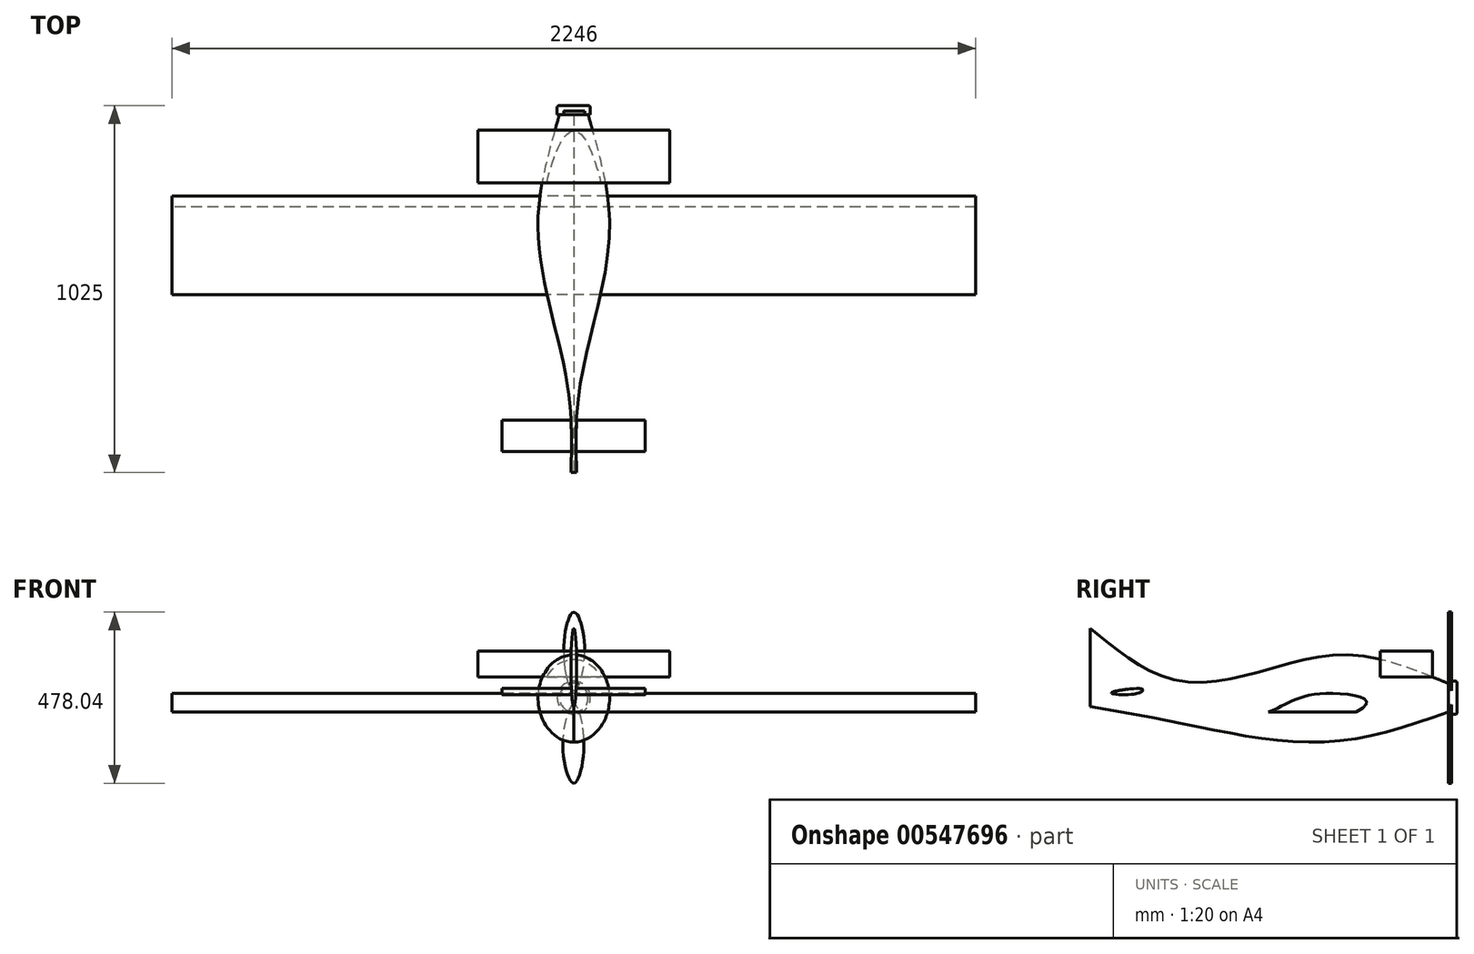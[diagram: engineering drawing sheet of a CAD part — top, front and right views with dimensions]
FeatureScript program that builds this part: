
annotation { "Feature Type Name" : "Feature", "Feature Type Description" : "" }
export const myFeature = defineFeature(function(context is Context, id is Id, definition is map)
    precondition{}
    {
        {
            var Q0;
            Q0=qCreatedBy(makeId("Front.planeOp"),FACE);
            cPlane(context, id + "F0", {"entities" : qUnion([Q0]), "cplaneType" : CPlaneType.OFFSET, "offset" : 300 * mm, "width" : 150 * mm, "height" : 150 * mm});
        }
        {
            var Q0;
            Q0=qCreatedBy(makeId("Front.planeOp"),FACE);
            cPlane(context, id + "F1", {"entities" : qUnion([Q0]), "cplaneType" : CPlaneType.OFFSET, "offset" : 800 * mm, "width" : 150 * mm, "height" : 150 * mm});
        }
        {
            var Q0;
            Q0=qCreatedBy(makeId("Front.planeOp"),FACE);
            cPlane(context, id + "F2", {"entities" : qUnion([Q0]), "cplaneType" : CPlaneType.OFFSET, "offset" : 1000 * mm, "width" : 150 * mm, "height" : 150 * mm});
        }
        {
            var Q0;
            Q0=qCreatedBy(makeId("Front.planeOp"),FACE);
            var sketch = newSketch(context, id + "F3", { "sketchPlane" : qUnion([Q0])});
            skCircle(sketch, "E0", {"center": v(0, 0) * mm, "radius": 40 * mm});
            skSolve(sketch);
        }
        {
            var Q0;
            Q0=qCreatedBy(id+"F0.planeOp",FACE);
            var sketch = newSketch(context, id + "F4", { "sketchPlane" : qUnion([Q0])});
            skEllipse(sketch, "E1", {"center": v(0, 0) * mm, "majorRadius": 120 * mm, "minorRadius": 100 * mm, "majorAxis": v(0, 1)});
            skSolve(sketch);
        }
        {
            var Q0;
            Q0=qCreatedBy(id+"F1.planeOp",FACE);
            var sketch = newSketch(context, id + "F5", { "sketchPlane" : qUnion([Q0])});
            skEllipse(sketch, "E2", {"center": v(0, 0) * mm, "majorRadius": 60.26 * mm, "minorRadius": 11.72 * mm, "majorAxis": v(0, 1)});
            skSolve(sketch);
        }
        {
            var Q0;
            Q0=qCreatedBy(id+"F2.planeOp",FACE);
            var sketch = newSketch(context, id + "F6", { "sketchPlane" : qUnion([Q0])});
            skEllipse(sketch, "E3", {"center": v(0, 84.1) * mm, "majorRadius": 109.22 * mm, "minorRadius": 7.91 * mm, "majorAxis": v(0, -1)});
            skSolve(sketch);
        }
        {
            var Q0;
            Q0=makeQuery(id+"F3.imprint","IMPRINT",FACE,{"disambiguationData":[TD([[makeQuery(id+"F3.imprint","IMPRINT",EDGE,{"derivedFrom":sQuery(id+"F3.wireOp",EDGE,"E0")}),1.0]])]});
            var Q1;
            Q1=makeQuery(id+"F4.imprint","IMPRINT",FACE,{"disambiguationData":[TD([[makeQuery(id+"F4.imprint","IMPRINT",EDGE,{"derivedFrom":sQuery(id+"F4.wireOp",EDGE,"E1")}),1.0]])]});
            var Q2;
            Q2=makeQuery(id+"F5.imprint","IMPRINT",FACE,{"disambiguationData":[TD([[makeQuery(id+"F5.imprint","IMPRINT",EDGE,{"derivedFrom":sQuery(id+"F5.wireOp",EDGE,"E2")}),1.0]])]});
            var Q3;
            Q3=makeQuery(id+"F6.imprint","IMPRINT",FACE,{"disambiguationData":[TD([[makeQuery(id+"F6.imprint","IMPRINT",EDGE,{"derivedFrom":sQuery(id+"F6.wireOp",EDGE,"E3")}),1.0]])]});
            loft(context, id + "F7", {"sheetProfilesArray" : [{ "sheetProfileEntities" : qUnion([Q0]) }, { "sheetProfileEntities" : qUnion([Q1]) }, { "sheetProfileEntities" : qUnion([Q2]) }, { "sheetProfileEntities" : qUnion([Q3]) }]});
        }
        {
            var Q0;
            Q0=qCreatedBy(makeId("Right.planeOp"),FACE);
            var sketch = newSketch(context, id + "F8", { "sketchPlane" : qUnion([Q0])});
            skLineSegment(sketch, "E4", {"start": v(-257.56, -39.92) * mm, "end": v(-502.8, -39.92) * mm});
            skFitSpline(sketch, "E5", {"points": [v(-257.56, -39.92) * mm, v(-337.4, 11.94) * mm, v(-502.8, -39.92) * mm], "startDerivative": vector(561.41, 281.39) * mm, "endDerivative": vector(-318.12, -122.75) * mm});
            skSolve(sketch);
        }
        {
            var Q0;
            Q0=makeQuery(id+"F8.imprint","IMPRINT",FACE,{"disambiguationData":[TD([[makeQuery(id+"F8.imprint","IMPRINT",EDGE,{"derivedFrom":sQuery(id+"F8.wireOp",EDGE,"E4")}),-1.0]])]});
            extrude(context, id + "F9", {"entities" : qUnion([Q0]), "endBound" : BoundingType.SYMMETRIC, "depth" : 2246 * mm, "offsetDistance" : 25 * mm});
        }
        {
            var Q0;
            Q0=qCreatedBy(makeId("Front.planeOp"),FACE);
            var sketch = newSketch(context, id + "F10", { "sketchPlane" : qUnion([Q0])});
            skCircle(sketch, "E6", {"center": v(0, 0) * mm, "radius": 46.37 * mm});
            skSolve(sketch);
        }
        {
            var Q0;
            Q0=makeQuery(id+"F10.imprint","IMPRINT",FACE,{"disambiguationData":[TD([[makeQuery(id+"F10.imprint","IMPRINT",EDGE,{"derivedFrom":sQuery(id+"F10.wireOp",EDGE,"E6")}),1.0]])]});
            extrude(context, id + "F11", {"entities" : qUnion([Q0]), "oppositeDirection" : true, "depth" : 25 * mm, "offsetDistance" : 25 * mm});
        }
        {
            var Q0;
            Q0=makeQuery(id+"F11.opExtrude","CAP_EDGE",EDGE,{"disambiguationData":[OSD([sQuery(id+"F10.wireOp",EDGE,"E6")])],"isStart":false});
            fillet(context, id + "F12", {"entities" : qUnion([Q0]), "radius" : 5 * mm, "tangentPropagation" : true, "allowEdgeOverflow" : false});
        }
        {
            var Q0;
            Q0=qCreatedBy(makeId("Front.planeOp"),FACE);
            var sketch = newSketch(context, id + "F13", { "sketchPlane" : qUnion([Q0])});
            skFitSpline(sketch, "E7", {"points": [v(0, 19.56) * mm, v(30.67, 130.03) * mm, v(0, 239.02) * mm, v(-28.3, 124.8) * mm, v(0, 19.56) * mm]});
            skSolve(sketch);
        }
        {
            var Q0;
            Q0=makeQuery(id+"F13.imprint","IMPRINT",FACE,{"disambiguationData":[TD([[makeQuery(id+"F13.imprint","IMPRINT",EDGE,{"derivedFrom":sQuery(id+"F13.wireOp",EDGE,"E7")}),1.0]])]});
            extrude(context, id + "F14", {"entities" : qUnion([Q0]), "oppositeDirection" : true, "depth" : 10 * mm, "offsetDistance" : 25 * mm});
        }
        {
            var Q0;
            Q0=qCreatedBy(makeId("Right.planeOp"),FACE);
            var sketch = newSketch(context, id + "F15", { "sketchPlane" : qUnion([Q0])});
            skLineSegment(sketch, "E8", {"start": v(0, 0) * mm, "end": v(243.34, 0) * mm, "construction": true});
            skSolve(sketch);
        }
        {
            var Q0;
            Q0=makeQuery(id+"F14.opExtrude","SWEPT_BODY",BODY,{"disambiguationData":[OSD([sQuery(id+"F13.wireOp",EDGE,"E7")])]});
            var Q1;
            Q1=sQuery(id+"F15.wireOp",EDGE,"E8");
            circularPattern(context, id + "F16", {"entities" : qUnion([Q0]), "axis" : qUnion([Q1]), "angle" : 360 * degree, "instanceCount" : 2, "equalSpace" : true});
        }
        {
            var Q0;
            Q0=qCreatedBy(makeId("Right.planeOp"),FACE);
            var sketch = newSketch(context, id + "F17", { "sketchPlane" : qUnion([Q0])});
            skLineSegment(sketch, "E9.bottom", {"start": v(-43.3, 129.88) * mm, "end": v(-190.34, 129.88) * mm});
            skLineSegment(sketch, "E9.top", {"start": v(-43.3, 58.22) * mm, "end": v(-190.34, 58.22) * mm});
            skLineSegment(sketch, "E9.left", {"start": v(-43.3, 129.88) * mm, "end": v(-43.3, 58.22) * mm});
            skLineSegment(sketch, "E9.right", {"start": v(-190.34, 129.88) * mm, "end": v(-190.34, 58.22) * mm});
            skSolve(sketch);
        }
        {
            var Q0;
            Q0=makeQuery(id+"F17.imprint","IMPRINT",FACE,{"disambiguationData":[TD([[makeQuery(id+"F17.imprint","IMPRINT",EDGE,{"derivedFrom":sQuery(id+"F17.wireOp",EDGE,"E9.bottom")}),1.0]])]});
            extrude(context, id + "F18", {"entities" : qUnion([Q0]), "endBound" : BoundingType.SYMMETRIC, "depth" : 536 * mm, "offsetDistance" : 25 * mm});
        }
        {
            var Q0;
            Q0=makeQuery(id+"F18.opExtrude","SWEPT_BODY",BODY,{"disambiguationData":[OSD([sQuery(id+"F17.wireOp",EDGE,"E9.bottom"),sQuery(id+"F17.wireOp",EDGE,"E9.top"),sQuery(id+"F17.wireOp",EDGE,"E9.left"),sQuery(id+"F17.wireOp",EDGE,"E9.right")])]});
            var Q1;
            Q1=makeQuery(id+"F7.opLoft","SWEPT_BODY",BODY,{"disambiguationData":[OSD([makeQuery(id+"F3.imprint","IMPRINT",FACE,{"disambiguationData":[TD([[makeQuery(id+"F3.imprint","IMPRINT",EDGE,{"derivedFrom":sQuery(id+"F3.wireOp",EDGE,"E0")}),1.0]])]}),sQuery(id+"F4.wireOp",EDGE,"E1"),sQuery(id+"F5.wireOp",EDGE,"E2"),makeQuery(id+"F6.imprint","IMPRINT",FACE,{"disambiguationData":[TD([[makeQuery(id+"F6.imprint","IMPRINT",EDGE,{"derivedFrom":sQuery(id+"F6.wireOp",EDGE,"E3")}),1.0]])]})])]});
            booleanBodies(context, id + "F19", {"operationType" : BooleanOperationType.INTERSECTION, "tools" : qUnion([Q0, Q1]), "keepTools" : true});
        }
        {
            var Q0;
            Q0=qCreatedBy(makeId("Right.planeOp"),FACE);
            var sketch = newSketch(context, id + "F20", { "sketchPlane" : qUnion([Q0])});
            skFitSpline(sketch, "E10", {"points": [v(-940.4, 12.59) * mm, v(-867.01, 12.54) * mm, v(-853.86, 23.2) * mm, v(-916.18, 20.85) * mm, v(-940.4, 12.59) * mm]});
            skSolve(sketch);
        }
        {
            var Q0;
            Q0 = qSketchRegion(id + "F20", true);
            extrude(context, id + "F21", {"entities" : qUnion([Q0]), "operationType" : NewBodyOperationType.ADD, "endBound" : BoundingType.SYMMETRIC, "depth" : 400 * mm, "offsetDistance" : 25 * mm});
        }
    });
